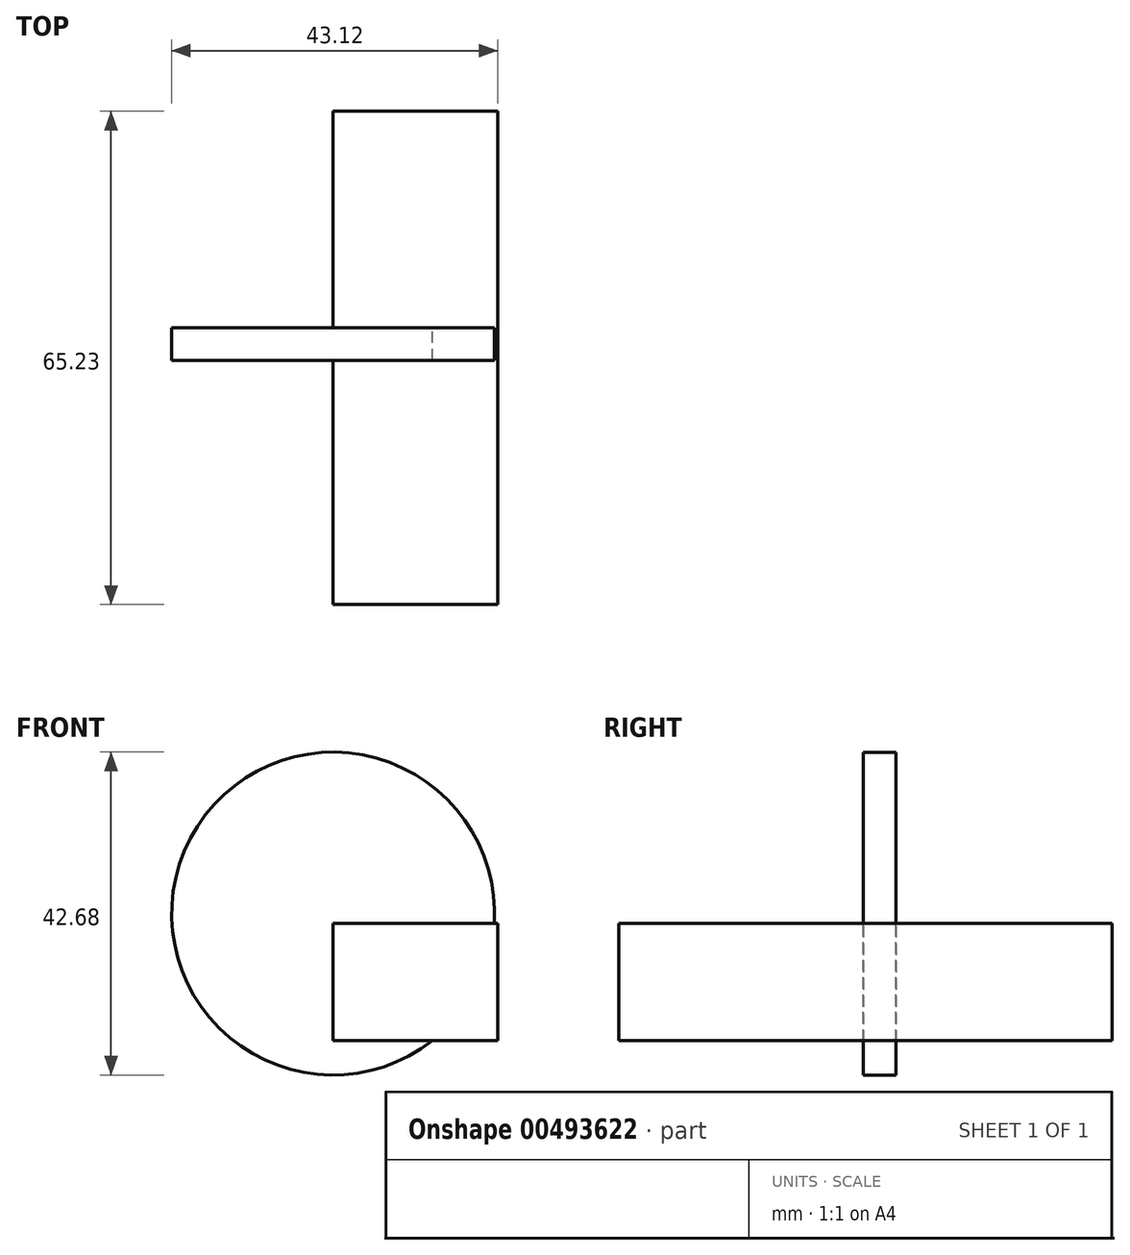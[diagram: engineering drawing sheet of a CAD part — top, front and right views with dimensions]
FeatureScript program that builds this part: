
annotation { "Feature Type Name" : "Feature", "Feature Type Description" : "" }
export const myFeature = defineFeature(function(context is Context, id is Id, definition is map)
    precondition{}
    {
        {
            var Q0;
            Q0=qCreatedBy(makeId("Front.planeOp"),FACE);
            var sketch = newSketch(context, id + "F0", { "sketchPlane" : qUnion([Q0])});
            skCircle(sketch, "E0", {"center": v(0, 16.8) * mm, "radius": 21.34 * mm});
            skSolve(sketch);
        }
        {
            var Q0;
            Q0 = qSketchRegion(id + "F0", true);
            extrude(context, id + "F1", {"entities" : qUnion([Q0]), "depth" : 4.32 * mm});
        }
        {
            var Q0;
            Q0=qCreatedBy(makeId("Top.planeOp"),FACE);
            var sketch = newSketch(context, id + "F2", { "sketchPlane" : qUnion([Q0])});
            skLineSegment(sketch, "E1.bottom", {"start": v(0, 28.6) * mm, "end": v(21.78, 28.6) * mm});
            skLineSegment(sketch, "E1.top", {"start": v(0, -36.63) * mm, "end": v(21.78, -36.63) * mm});
            skLineSegment(sketch, "E1.left", {"start": v(0, 28.6) * mm, "end": v(0, -36.63) * mm});
            skLineSegment(sketch, "E1.right", {"start": v(21.78, 28.6) * mm, "end": v(21.78, -36.63) * mm});
            skSolve(sketch);
        }
        {
            var Q0;
            Q0 = qSketchRegion(id + "F2", true);
            var Q1;
            Q1=makeQuery(id+"F2.imprint","IMPRINT",FACE,{"disambiguationData":[TD([[makeQuery(id+"F2.imprint","IMPRINT",EDGE,{"derivedFrom":sQuery(id+"F2.wireOp",EDGE,"E1.bottom")}),-1.0]])]});
            extrude(context, id + "F3", {"entities" : qUnion([Q0, Q1]), "operationType" : NewBodyOperationType.ADD, "depth" : 15.5 * mm});
        }
    });
